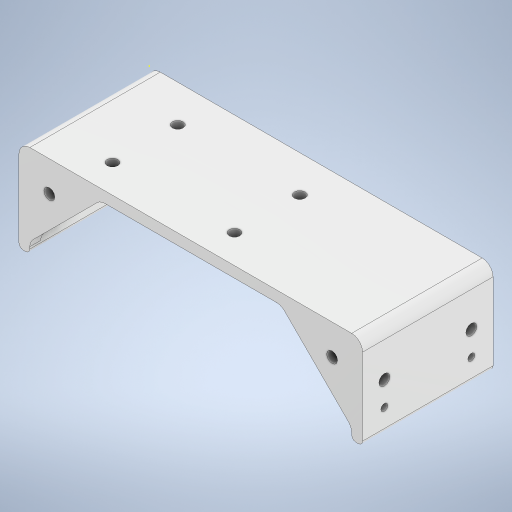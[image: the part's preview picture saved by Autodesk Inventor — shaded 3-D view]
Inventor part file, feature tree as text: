
AUTODESK INVENTOR PART (.ipt)
format: ipt  version: 2024.3 (Build 283343000, 343)  size: 466,944 bytes
history: native  units: mm
features: sketch x12, extrude x8, fillet x3, hole x2, projected_geometry x2, other x1
ambient origin geometry x8: Origin, YZ Plane, XZ Plane, XY Plane, X Axis, Y Axis, Z Axis, Center Point
bodies: Body1 (feature_tree)
feature tree (28):
  other  "ソリッド1"
  extrude  "押し出し1"  Depth=158.0mm
  extrude  "押し出し3"  Depth=250.0mm
  extrude  "押し出し4"  Depth=5.0mm
  hole  "穴2"  [1 undecoded]
  extrude  "押し出し5"  Depth=50.0mm
  extrude  "押し出し6"  Depth=50.0mm
  extrude  "押し出し7"  Depth=30.0mm
  fillet  "フィレット4"  Radius=5.0mm
  fillet  "フィレット6"  Radius=50.0mm
  extrude  "押し出し8"  Depth=50.0mm
  fillet  "フィレット7"  Radius=30.0mm
  sketch  "スケッチ13"
  sketch  "スケッチ14"
  hole  "穴3"  [1 undecoded]
  extrude  "押し出し9"  Depth=5.0mm TaperAngle=0.0deg
  sketch  "スケッチ1"
  sketch  "スケッチ5"
  sketch  "スケッチ6"
  sketch  "スケッチ7"
  sketch  "スケッチ8"
  sketch  "スケッチ9"
  sketch  "スケッチ10"
  sketch  "スケッチ12"
  projected_geometry  "投影ループ1"
  sketch  "スケッチ15"
  sketch  "スケッチ16"
  projected_geometry  "投影ループ2"
note: 2 required parameter values undecoded (feature->parameter linkage not recoverable at this tier; creation-order binding heuristic only, values carry confidence <= 0.55)
